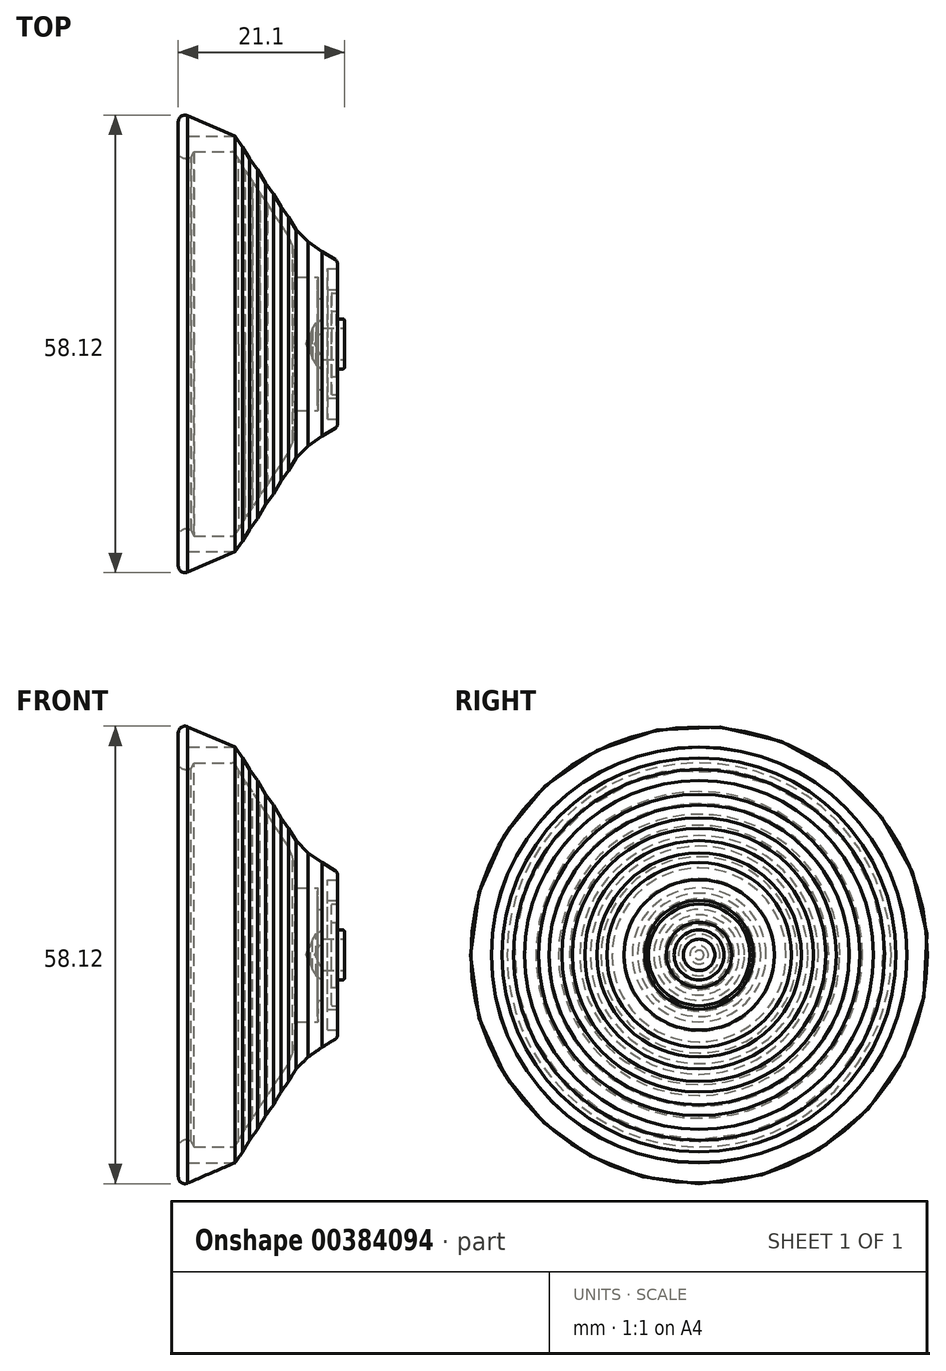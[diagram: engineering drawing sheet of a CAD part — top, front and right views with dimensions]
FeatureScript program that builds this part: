
annotation { "Feature Type Name" : "Feature", "Feature Type Description" : "" }
export const myFeature = defineFeature(function(context is Context, id is Id, definition is map)
    precondition{}
    {
        {
            var Q0;
            Q0=qCreatedBy(makeId("Front.planeOp"),FACE);
            var sketch = newSketch(context, id + "F0", { "sketchPlane" : qUnion([Q0])});
            skLineSegment(sketch, "E0", {"start": v(-1.4, 2) * mm, "end": v(-4.2, 2) * mm});
            skLineSegment(sketch, "E1", {"start": v(-4.2, 2) * mm, "end": v(-5.19, 0) * mm});
            skLineSegment(sketch, "E2", {"start": v(-5.19, 0) * mm, "end": v(-6.3, 0) * mm});
            skLineSegment(sketch, "E3", {"start": v(-9.41, 15.16) * mm, "end": v(-15.43, 24.4) * mm});
            skLineSegment(sketch, "E4", {"start": v(-22.5, 24.5) * mm, "end": v(-22.5, 29.5) * mm});
            skLineSegment(sketch, "E5", {"start": v(-1.4, 3.17) * mm, "end": v(-2.4, 3.17) * mm});
            skLineSegment(sketch, "E6", {"start": v(-2.4, 3.17) * mm, "end": v(-2.4, 4.15) * mm});
            skLineSegment(sketch, "E7", {"start": v(-2.4, 4.15) * mm, "end": v(-3.05, 4.15) * mm});
            skLineSegment(sketch, "E8", {"start": v(-3.05, 4.15) * mm, "end": v(-3.05, 6.45) * mm});
            skLineSegment(sketch, "E9", {"start": v(-3.05, 6.45) * mm, "end": v(-2.25, 6.45) * mm});
            skLineSegment(sketch, "E10", {"start": v(-2.25, 6.45) * mm, "end": v(-2.25, 6.9) * mm});
            skLineSegment(sketch, "E11", {"start": v(-2.25, 6.9) * mm, "end": v(-3.55, 6.9) * mm});
            skLineSegment(sketch, "E12", {"start": v(-3.55, 6.9) * mm, "end": v(-3.55, 9.55) * mm});
            skLineSegment(sketch, "E13", {"start": v(-3.55, 9.55) * mm, "end": v(-2.3, 9.55) * mm});
            skLineSegment(sketch, "E14", {"start": v(-2.3, 9.55) * mm, "end": v(-2.3, 10.55) * mm});
            skLineSegment(sketch, "E15", {"start": v(-1.4, 3.17) * mm, "end": v(-1.4, 2) * mm});
            skLineSegment(sketch, "E16", {"start": v(-2.3, 10.55) * mm, "end": v(-2.3, 10.55) * mm});
            skPoint(sketch, "E17.visualSharp", {"position": v(-16.5, 26.05) * mm});
            skPoint(sketch, "E18.visualSharp", {"position": v(-22.5, 21.16) * mm});
            skArc(sketch, "E18.filletArc", {"start": v(-22.5, 24.5) * mm, "mid": v(-21.95, 23.6) * mm, "end": v(-20.9, 23.7) * mm});
            skLineSegment(sketch, "E19", {"start": v(-2.3, 10.55) * mm, "end": v(-4.25, 11.73) * mm});
            skLineSegment(sketch, "E20", {"start": v(-4.25, 11.73) * mm, "end": v(-6.02, 12.97) * mm});
            skLineSegment(sketch, "E21", {"start": v(-6.02, 12.97) * mm, "end": v(-7.56, 14.5) * mm});
            skLineSegment(sketch, "E22", {"start": v(-7.56, 14.5) * mm, "end": v(-15.3, 26.4) * mm});
            skLineSegment(sketch, "E23", {"start": v(-22.5, 29.5) * mm, "end": v(-21.3, 28.98) * mm});
            skLineSegment(sketch, "E24", {"start": v(-7.5, 9.7) * mm, "end": v(-7.5, 8.5) * mm});
            skLineSegment(sketch, "E25", {"start": v(-7.5, 8.5) * mm, "end": v(-4.75, 8.5) * mm});
            skLineSegment(sketch, "E26", {"start": v(-4.75, 5.77) * mm, "end": v(-4.25, 5.77) * mm});
            skLineSegment(sketch, "E27", {"start": v(-5, 2.64) * mm, "end": v(-4.25, 3.17) * mm});
            skLineSegment(sketch, "E28", {"start": v(-21.3, 28.98) * mm, "end": v(-21.3, 26.4) * mm});
            skLineSegment(sketch, "E29", {"start": v(-21.3, 26.4) * mm, "end": v(-15.3, 26.4) * mm});
            skLineSegment(sketch, "E30", {"start": v(-15.43, 24.4) * mm, "end": v(-20.5, 24.4) * mm});
            skLineSegment(sketch, "E31", {"start": v(-20.9, 23.7) * mm, "end": v(-20.5, 24.4) * mm});
            skPoint(sketch, "E32.visualSharp", {"position": v(-7.5, 12.22) * mm});
            skLineSegment(sketch, "E33", {"start": v(-7.5, 9.7) * mm, "end": v(-7.68, 11.04) * mm});
            skLineSegment(sketch, "E34", {"start": v(-7.68, 11.04) * mm, "end": v(-8.01, 12.47) * mm});
            skLineSegment(sketch, "E35", {"start": v(-8.01, 12.47) * mm, "end": v(-8.54, 13.81) * mm});
            skLineSegment(sketch, "E36", {"start": v(-8.54, 13.81) * mm, "end": v(-9.41, 15.16) * mm});
            skLineSegment(sketch, "E37", {"start": v(-9.41, 15.16) * mm, "end": v(-10.34, 16.47) * mm});
            skLineSegment(sketch, "E38", {"start": v(-10.34, 16.47) * mm, "end": v(-11.18, 17.87) * mm});
            skLineSegment(sketch, "E39", {"start": v(-11.18, 17.87) * mm, "end": v(-12.14, 19.22) * mm});
            skLineSegment(sketch, "E40", {"start": v(-12.14, 19.22) * mm, "end": v(-13.04, 20.73) * mm});
            skLineSegment(sketch, "E41", {"start": v(-13.04, 20.73) * mm, "end": v(-14.02, 22.1) * mm});
            skLineSegment(sketch, "E42", {"start": v(-14.02, 22.1) * mm, "end": v(-14.87, 23.54) * mm});
            skLineSegment(sketch, "E43", {"start": v(-7.56, 14.5) * mm, "end": v(-8.5, 16.1) * mm});
            skLineSegment(sketch, "E44", {"start": v(-8.5, 16.1) * mm, "end": v(-9.46, 17.43) * mm});
            skLineSegment(sketch, "E45", {"start": v(-9.46, 17.43) * mm, "end": v(-10.4, 19.05) * mm});
            skLineSegment(sketch, "E46", {"start": v(-10.4, 19.05) * mm, "end": v(-11.4, 20.4) * mm});
            skLineSegment(sketch, "E47", {"start": v(-11.4, 20.4) * mm, "end": v(-12.45, 22.16) * mm});
            skLineSegment(sketch, "E48", {"start": v(-12.45, 22.16) * mm, "end": v(-13.45, 23.56) * mm});
            skLineSegment(sketch, "E49", {"start": v(-13.45, 23.56) * mm, "end": v(-14.31, 25.02) * mm});
            skLineSegment(sketch, "E50", {"start": v(-14.31, 25.02) * mm, "end": v(-15.29, 26.38) * mm});
            skLineSegment(sketch, "E51", {"start": v(-4.75, 8.5) * mm, "end": v(-4.82, 7.82) * mm});
            skLineSegment(sketch, "E52", {"start": v(-4.82, 7.82) * mm, "end": v(-4.75, 7.16) * mm});
            skLineSegment(sketch, "E53", {"start": v(-4.75, 7.16) * mm, "end": v(-4.82, 6.48) * mm});
            skLineSegment(sketch, "E54", {"start": v(-4.82, 6.48) * mm, "end": v(-4.75, 5.77) * mm});
            skLineSegment(sketch, "E55", {"start": v(-4.25, 5.77) * mm, "end": v(-4.32, 5.08) * mm});
            skLineSegment(sketch, "E56", {"start": v(-4.32, 5.08) * mm, "end": v(-4.25, 4.44) * mm});
            skLineSegment(sketch, "E57", {"start": v(-4.25, 4.44) * mm, "end": v(-4.3, 3.83) * mm});
            skLineSegment(sketch, "E58", {"start": v(-4.3, 3.83) * mm, "end": v(-4.25, 3.17) * mm});
            skLineSegment(sketch, "E59", {"start": v(-6.3, 0) * mm, "end": v(-6.08, 0.6) * mm});
            skLineSegment(sketch, "E60", {"start": v(-6.08, 0.6) * mm, "end": v(-5.73, 1.16) * mm});
            skLineSegment(sketch, "E61", {"start": v(-5.73, 1.16) * mm, "end": v(-5.45, 1.93) * mm});
            skLineSegment(sketch, "E62", {"start": v(-5.45, 1.93) * mm, "end": v(-5, 2.64) * mm});
            skSolve(sketch);
        }
        {
            var Q0;
            Q0=qSketchRegion(id+"F0",true);
            var Q1;
            Q1=sQuery(id+"F0.wireOp",EDGE,"E2");
            revolve(context, id + "F1", {"entities" : qUnion([Q0]), "axis" : qUnion([Q1]), "revolveType" : RevolveType.FULL});
        }
        {
            var Q0;
            Q0=makeQuery(id+"F1.opRevolve","SWEPT_EDGE",EDGE,{"disambiguationData":[OSD([sQuery(id+"F0.wireOp",EDGE,"E6"),sQuery(id+"F0.wireOp",EDGE,"E7")])]});
            var Q1;
            Q1=makeQuery(id+"F1.opRevolve","SWEPT_EDGE",EDGE,{"disambiguationData":[OSD([sQuery(id+"F0.wireOp",EDGE,"E7"),sQuery(id+"F0.wireOp",EDGE,"E8")])]});
            var Q2;
            Q2=makeQuery(id+"F1.opRevolve","SWEPT_EDGE",EDGE,{"disambiguationData":[OSD([sQuery(id+"F0.wireOp",EDGE,"E9"),sQuery(id+"F0.wireOp",EDGE,"E10")])]});
            var Q3;
            Q3=makeQuery(id+"F1.opRevolve","SWEPT_EDGE",EDGE,{"disambiguationData":[OSD([sQuery(id+"F0.wireOp",EDGE,"E10"),sQuery(id+"F0.wireOp",EDGE,"E11")])]});
            var Q4;
            Q4=makeQuery(id+"F1.opRevolve","SWEPT_EDGE",EDGE,{"disambiguationData":[OSD([sQuery(id+"F0.wireOp",EDGE,"E13"),sQuery(id+"F0.wireOp",EDGE,"E14")])]});
            var Q5;
            Q5=makeQuery(id+"F1.opRevolve","SWEPT_EDGE",EDGE,{"disambiguationData":[OSD([sQuery(id+"F0.wireOp",EDGE,"E8"),sQuery(id+"F0.wireOp",EDGE,"E9")])]});
            var Q6;
            Q6=makeQuery(id+"F1.opRevolve","SWEPT_EDGE",EDGE,{"disambiguationData":[OSD([sQuery(id+"F0.wireOp",EDGE,"E5"),sQuery(id+"F0.wireOp",EDGE,"E6")])]});
            fillet(context, id + "F2", {"entities" : qUnion([Q0, Q1, Q2, Q3, Q4, Q5, Q6]), "radius" : 0.1 * mm, "tangentPropagation" : true, "allowEdgeOverflow" : false});
        }
        {
            var Q0;
            Q0=makeQuery(id+"F1.opRevolve","SWEPT_EDGE",EDGE,{"disambiguationData":[OSD([sQuery(id+"F0.wireOp",EDGE,"E5"),sQuery(id+"F0.wireOp",EDGE,"E15")])]});
            fillet(context, id + "F3", {"entities" : qUnion([Q0]), "radius" : 0.2 * mm, "tangentPropagation" : true, "allowEdgeOverflow" : false});
        }
        {
            var Q0;
            Q0=makeQuery(id+"F1.opRevolve","SWEPT_EDGE",EDGE,{"disambiguationData":[OSD([sQuery(id+"F0.wireOp",EDGE,"E3"),sQuery(id+"F0.wireOp",EDGE,"E30")])]});
            fillet(context, id + "F4", {"entities" : qUnion([Q0]), "radius" : 0.5 * mm, "tangentPropagation" : true, "allowEdgeOverflow" : false});
        }
        {
            var Q0;
            Q0=makeQuery(id+"F1.opRevolve","SWEPT_EDGE",EDGE,{"disambiguationData":[OSD([sQuery(id+"F0.wireOp",EDGE,"E14"),sQuery(id+"F0.wireOp",EDGE,"E19")])]});
            fillet(context, id + "F5", {"entities" : qUnion([Q0]), "radius" : 0.5 * mm, "tangentPropagation" : true, "allowEdgeOverflow" : false});
        }
        {
            var Q0;
            Q0=qCreatedBy(makeId("Front.planeOp"),FACE);
            var sketch = newSketch(context, id + "F6", { "sketchPlane" : qUnion([Q0])});
            skLineSegment(sketch, "E63", {"start": v(-21.3, 26.4) * mm, "end": v(-15.3, 26.4) * mm});
            skLineSegment(sketch, "E64.0", {"start": v(-21.3, 28.98) * mm, "end": v(-21.3, -28.98) * mm});
            skLineSegment(sketch, "E65", {"start": v(-21.3, 28.98) * mm, "end": v(-15.3, 26.4) * mm});
            skLineSegment(sketch, "E66", {"start": v(-21.3, 26.4) * mm, "end": v(-21.3, 28.98) * mm});
            skPoint(sketch, "E67.endSnap0", {"position": v(-21.3, 0) * mm});
            skLineSegment(sketch, "E68", {"start": v(-22.1, 29.33) * mm, "end": v(-21.3, 28.98) * mm});
            skLineSegment(sketch, "E69", {"start": v(0, 0) * mm, "end": v(-27.4, 0) * mm});
            skSolve(sketch);
        }
        {
            var Q0;
            Q0=makeQuery(id+"F6.imprint","IMPRINT",FACE,{"disambiguationData":[TD([[makeQuery(id+"F6.imprint","IMPRINT",EDGE,{"derivedFrom":sQuery(id+"F6.wireOp",EDGE,"E63")}),1.0]])]});
            var Q1;
            Q1=sQuery(id+"F6.wireOp",EDGE,"E69");
            revolve(context, id + "F7", {"entities" : qUnion([Q0]), "axis" : qUnion([Q1]), "revolveType" : RevolveType.FULL});
        }
        {
            var Q0;
            Q0=makeQuery(id+"F1.opRevolve","SWEPT_EDGE",EDGE,{"disambiguationData":[OSD([sQuery(id+"F0.wireOp",EDGE,"E4"),sQuery(id+"F0.wireOp",EDGE,"qcfS0AuZ-xKJO-e0qy-MTLN-h3hrmbb2rTTs")])]});
            fillet(context, id + "F8", {"entities" : qUnion([Q0]), "radius" : 0.85 * mm, "tangentPropagation" : true, "allowEdgeOverflow" : false});
        }
    });
